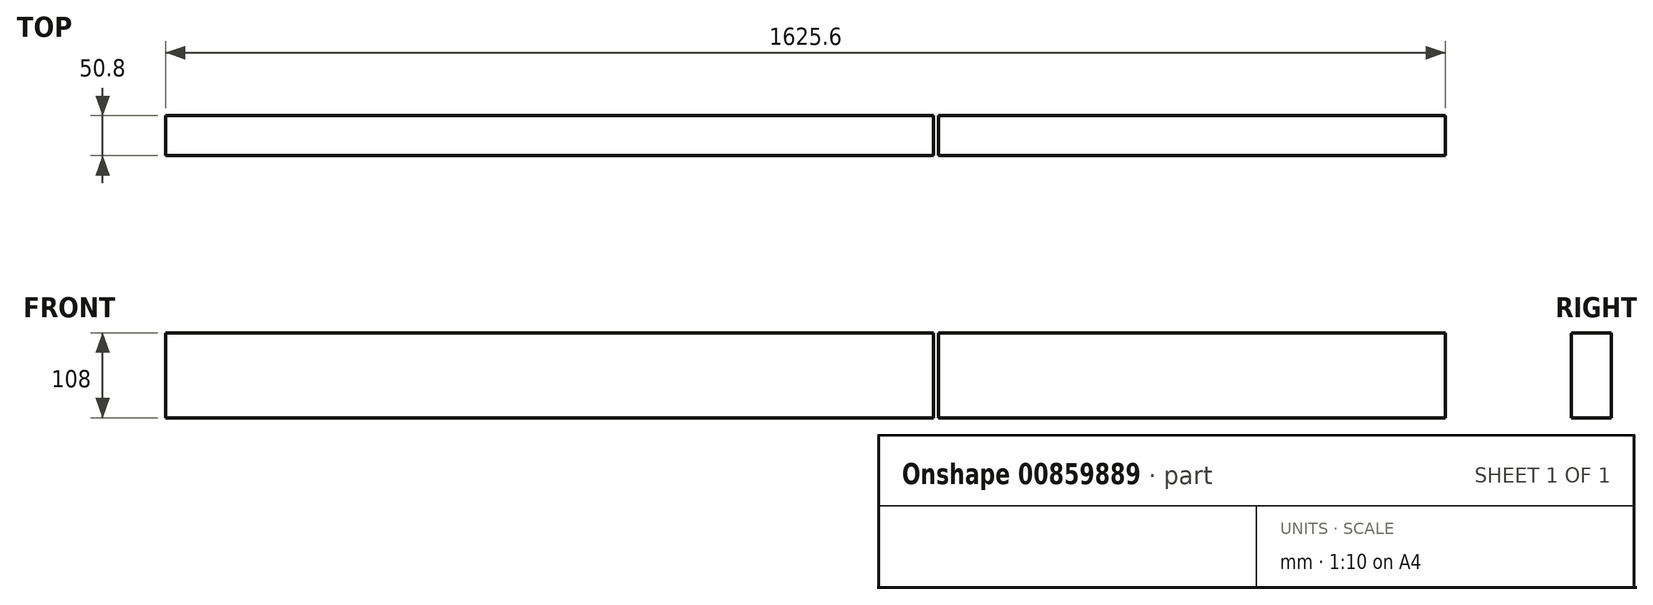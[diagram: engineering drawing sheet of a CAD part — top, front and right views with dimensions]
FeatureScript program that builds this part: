
annotation { "Feature Type Name" : "Feature", "Feature Type Description" : "" }
export const myFeature = defineFeature(function(context is Context, id is Id, definition is map)
    precondition{}
    {
        {
            assignVariable(context, id + "F0", {"name" : "TotalHeight", "anyValue" : 108});
        }
        {
            var Q0;
            Q0=qCreatedBy(makeId("Top.planeOp"),FACE);
            var sketch = newSketch(context, id + "F1", { "sketchPlane" : qUnion([Q0])});
            skLineSegment(sketch, "E0", {"start": v(0, 0) * mm, "end": v(-812.8, 0) * mm, "construction": true});
            skLineSegment(sketch, "E1.bottom", {"start": v(-812.8, 0) * mm, "end": v(162.56, 0) * mm});
            skLineSegment(sketch, "E1.top", {"start": v(-812.8, 50.8) * mm, "end": v(162.56, 50.8) * mm});
            skLineSegment(sketch, "E1.left", {"start": v(-812.8, 0) * mm, "end": v(-812.8, 50.8) * mm});
            skLineSegment(sketch, "E1.right", {"start": v(162.56, 0) * mm, "end": v(162.56, 50.8) * mm});
            skLineSegment(sketch, "E2", {"start": v(162.56, 0) * mm, "end": v(168.91, 0) * mm});
            skLineSegment(sketch, "E3.bottom", {"start": v(168.91, 0) * mm, "end": v(812.8, 0) * mm});
            skLineSegment(sketch, "E3.top", {"start": v(168.91, 50.8) * mm, "end": v(812.8, 50.8) * mm});
            skLineSegment(sketch, "E3.left", {"start": v(168.91, 0) * mm, "end": v(168.91, 50.8) * mm});
            skLineSegment(sketch, "E3.right", {"start": v(812.8, 0) * mm, "end": v(812.8, 50.8) * mm});
            skSolve(sketch);
        }
        {
            var Q0;
            Q0=makeQuery(id+"F1.imprint","IMPRINT",FACE,{"disambiguationData":[TD([[makeQuery(id+"F1.imprint","IMPRINT",EDGE,{"derivedFrom":sQuery(id+"F1.wireOp",EDGE,"E1.bottom")}),1.0]])]});
            var Q1;
            Q1=makeQuery(id+"F1.imprint","IMPRINT",FACE,{"disambiguationData":[TD([[makeQuery(id+"F1.imprint","IMPRINT",EDGE,{"derivedFrom":sQuery(id+"F1.wireOp",EDGE,"E3.bottom")}),1.0]])]});
            extrude(context, id + "F2", {"entities" : qUnion([Q0, Q1]), "depth" : (getVariable(context, 'TotalHeight')) * mm, "offsetDistance" : 25.4 * mm});
        }
        {
            var Q0;
            Q0=makeQuery(id+"F2.opExtrude","SWEPT_FACE",FACE,{"disambiguationData":[OSD([sQuery(id+"F1.wireOp",EDGE,"E1.bottom")])]});
            var sketch = newSketch(context, id + "F3", { "sketchPlane" : qUnion([Q0])});
            skLineSegment(sketch, "E4", {"start": v(-812.8, 1645.92) * mm, "end": v(162.56, 1645.92) * mm, "construction": true});
            skCircle(sketch, "E5", {"center": v(-325.12, 1645.92) * mm, "radius": 254 * mm});
            skSolve(sketch);
        }
        {
            var Q0;
            Q0=makeQuery(id+"F3.imprint","IMPRINT",FACE,{"disambiguationData":[TD([[makeQuery(id+"F3.imprint","IMPRINT",EDGE,{"derivedFrom":sQuery(id+"F3.wireOp",EDGE,"E5")}),1.0]])]});
            extrude(context, id + "F4", {"entities" : qUnion([Q0]), "operationType" : NewBodyOperationType.REMOVE, "endBound" : BoundingType.THROUGH_ALL, "oppositeDirection" : true, "depth" : 149.86 * mm, "offsetDistance" : 25.4 * mm});
        }
    });
